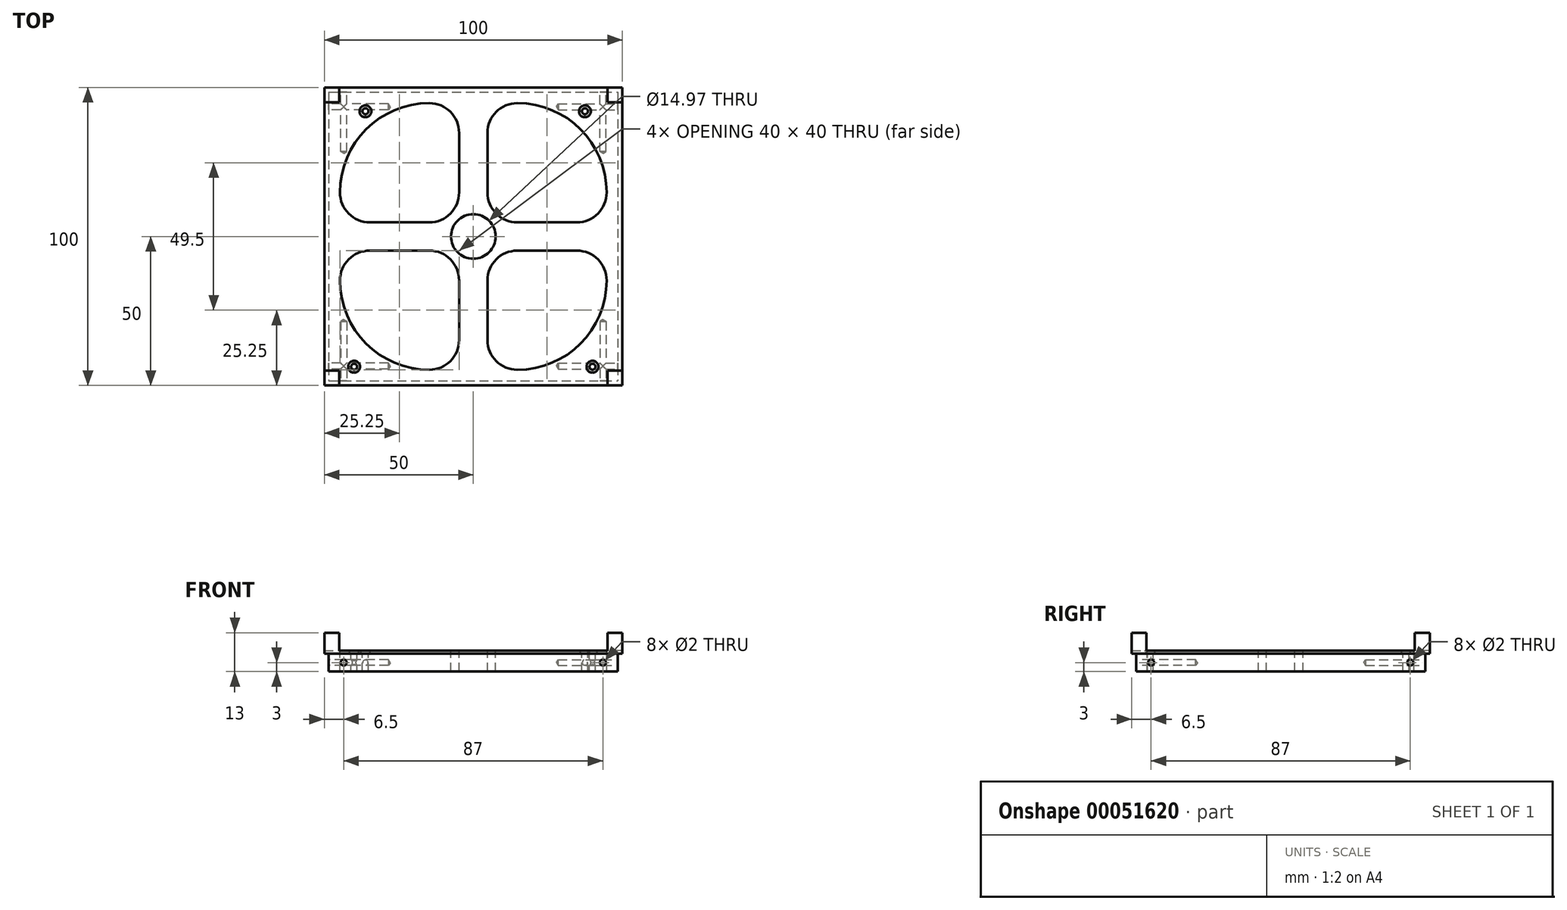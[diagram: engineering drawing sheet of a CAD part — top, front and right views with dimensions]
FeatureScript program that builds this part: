
annotation { "Feature Type Name" : "Feature", "Feature Type Description" : "" }
export const myFeature = defineFeature(function(context is Context, id is Id, definition is map)
    precondition{}
    {
        {
            var Q0;
            Q0=qCreatedBy(makeId("Top.planeOp"),FACE);
            var sketch = newSketch(context, id + "F0", { "sketchPlane" : qUnion([Q0])});
            skLineSegment(sketch, "E0.rect.bottom", {"start": v(-50, 50) * mm, "end": v(50, 50) * mm});
            skLineSegment(sketch, "E0.rect.top", {"start": v(-50, -50) * mm, "end": v(50, -50) * mm});
            skLineSegment(sketch, "E0.rect.left", {"start": v(-50, 50) * mm, "end": v(-50, -50) * mm});
            skLineSegment(sketch, "E0.rect.right", {"start": v(50, 50) * mm, "end": v(50, -50) * mm});
            skPoint(sketch, "E0.rect.middle", {"position": v(0, 0) * mm});
            skLineSegment(sketch, "E1.rect.bottom", {"start": v(-48.5, 48.5) * mm, "end": v(48.5, 48.5) * mm});
            skLineSegment(sketch, "E1.rect.top", {"start": v(-48.5, -48.5) * mm, "end": v(48.5, -48.5) * mm});
            skLineSegment(sketch, "E1.rect.left", {"start": v(-48.5, 48.5) * mm, "end": v(-48.5, -48.5) * mm});
            skLineSegment(sketch, "E1.rect.right", {"start": v(48.5, 48.5) * mm, "end": v(48.5, -48.5) * mm});
            skLineSegment(sketch, "E2.rect.bottom", {"start": v(-14.75, 4.75) * mm, "end": v(-34.75, 4.75) * mm});
            skLineSegment(sketch, "E2.rect.top", {"start": v(-14.75, 44.75) * mm, "end": v(-14.75, 44.75) * mm});
            skLineSegment(sketch, "E2.rect.left", {"start": v(-4.75, 14.75) * mm, "end": v(-4.75, 34.75) * mm});
            skLineSegment(sketch, "E2.rect.right", {"start": v(-44.75, 14.75) * mm, "end": v(-44.75, 14.75) * mm});
            skPoint(sketch, "E2.rect.middle", {"position": v(-24.75, 24.75) * mm});
            skPoint(sketch, "E3.visualSharp", {"position": v(-44.75, 44.75) * mm});
            skArc(sketch, "E3.filletArc", {"start": v(-14.75, 44.75) * mm, "mid": v(-35.96, 35.96) * mm, "end": v(-44.75, 14.75) * mm});
            skPoint(sketch, "E4.visualSharp", {"position": v(-4.75, 44.75) * mm});
            skArc(sketch, "E4.filletArc", {"start": v(-4.75, 34.75) * mm, "mid": v(-7.68, 41.82) * mm, "end": v(-14.75, 44.75) * mm});
            skPoint(sketch, "E5.visualSharp", {"position": v(-4.75, 4.75) * mm});
            skArc(sketch, "E5.filletArc", {"start": v(-14.75, 4.75) * mm, "mid": v(-7.68, 7.68) * mm, "end": v(-4.75, 14.75) * mm});
            skPoint(sketch, "E6.visualSharp", {"position": v(-44.75, 4.75) * mm});
            skArc(sketch, "E6.filletArc", {"start": v(-44.75, 14.75) * mm, "mid": v(-41.82, 7.68) * mm, "end": v(-34.75, 4.75) * mm});
            skLineSegment(sketch, "E7.MirrorCS", {"start": v(4.75, 14.75) * mm, "end": v(4.75, 34.75) * mm});
            skArc(sketch, "E8.MirrorCS", {"start": v(4.75, 34.75) * mm, "mid": v(7.68, 41.82) * mm, "end": v(14.75, 44.75) * mm});
            skLineSegment(sketch, "E9.MirrorCS", {"start": v(14.75, 44.75) * mm, "end": v(14.75, 44.75) * mm});
            skArc(sketch, "E10.MirrorCS", {"start": v(14.75, 44.75) * mm, "mid": v(35.96, 35.96) * mm, "end": v(44.75, 14.75) * mm});
            skLineSegment(sketch, "E11.MirrorCS", {"start": v(44.75, 14.75) * mm, "end": v(44.75, 14.75) * mm});
            skArc(sketch, "E12.MirrorCS", {"start": v(44.75, 14.75) * mm, "mid": v(41.82, 7.68) * mm, "end": v(34.75, 4.75) * mm});
            skLineSegment(sketch, "E13.MirrorCS", {"start": v(14.75, 4.75) * mm, "end": v(34.75, 4.75) * mm});
            skArc(sketch, "E14.MirrorCS", {"start": v(14.75, 4.75) * mm, "mid": v(7.68, 7.68) * mm, "end": v(4.75, 14.75) * mm});
            skPoint(sketch, "E15.MirrorP", {"position": v(24.75, 24.75) * mm});
            skArc(sketch, "E16.MirrorCS", {"start": v(14.75, -4.75) * mm, "mid": v(7.68, -7.68) * mm, "end": v(4.75, -14.75) * mm});
            skLineSegment(sketch, "E17.MirrorCS", {"start": v(4.75, -14.75) * mm, "end": v(4.75, -34.75) * mm});
            skArc(sketch, "E18.MirrorCS", {"start": v(4.75, -34.75) * mm, "mid": v(7.68, -41.82) * mm, "end": v(14.75, -44.75) * mm});
            skLineSegment(sketch, "E19.MirrorCS", {"start": v(14.75, -44.75) * mm, "end": v(14.75, -44.75) * mm});
            skArc(sketch, "E20.MirrorCS", {"start": v(14.75, -44.75) * mm, "mid": v(35.96, -35.96) * mm, "end": v(44.75, -14.75) * mm});
            skLineSegment(sketch, "E21.MirrorCS", {"start": v(44.75, -14.75) * mm, "end": v(44.75, -14.75) * mm});
            skArc(sketch, "E22.MirrorCS", {"start": v(44.75, -14.75) * mm, "mid": v(41.82, -7.68) * mm, "end": v(34.75, -4.75) * mm});
            skLineSegment(sketch, "E23.MirrorCS", {"start": v(14.75, -4.75) * mm, "end": v(34.75, -4.75) * mm});
            skPoint(sketch, "E24.MirrorP", {"position": v(24.75, -24.75) * mm});
            skLineSegment(sketch, "E25.MirrorCS", {"start": v(-4.75, -14.75) * mm, "end": v(-4.75, -34.75) * mm});
            skArc(sketch, "E26.MirrorCS", {"start": v(-14.75, -4.75) * mm, "mid": v(-7.68, -7.68) * mm, "end": v(-4.75, -14.75) * mm});
            skLineSegment(sketch, "E27.MirrorCS", {"start": v(-14.75, -4.75) * mm, "end": v(-34.75, -4.75) * mm});
            skArc(sketch, "E28.MirrorCS", {"start": v(-44.75, -14.75) * mm, "mid": v(-41.82, -7.68) * mm, "end": v(-34.75, -4.75) * mm});
            skLineSegment(sketch, "E29.MirrorCS", {"start": v(-44.75, -14.75) * mm, "end": v(-44.75, -14.75) * mm});
            skArc(sketch, "E30.MirrorCS", {"start": v(-14.75, -44.75) * mm, "mid": v(-35.96, -35.96) * mm, "end": v(-44.75, -14.75) * mm});
            skLineSegment(sketch, "E31.MirrorCS", {"start": v(-14.75, -44.75) * mm, "end": v(-14.75, -44.75) * mm});
            skArc(sketch, "E32.MirrorCS", {"start": v(-4.75, -34.75) * mm, "mid": v(-7.68, -41.82) * mm, "end": v(-14.75, -44.75) * mm});
            skPoint(sketch, "E33.MirrorP", {"position": v(-24.75, -24.75) * mm});
            skPoint(sketch, "E34", {"position": v(42.5, -42.5) * mm});
            skPoint(sketch, "E35.MirrorP", {"position": v(-42.5, -42.5) * mm});
            skPoint(sketch, "E36.MirrorP", {"position": v(42.5, 42.5) * mm});
            skPoint(sketch, "E37.MirrorP", {"position": v(-42.5, 42.5) * mm});
            skCircle(sketch, "E38", {"center": v(0, 0) * mm, "radius": 7.48 * mm});
            skSolve(sketch);
        }
        {
            var Q0;
            Q0=makeQuery(id+"F0.imprint","IMPRINT",FACE,{"disambiguationData":[TD([[makeQuery(id+"F0.imprint","IMPRINT",EDGE,{"derivedFrom":sQuery(id+"F0.wireOp",EDGE,"E1.rect.bottom")}),-1.0]])]});
            extrude(context, id + "F1", {"entities" : qUnion([Q0]), "oppositeDirection" : true, "depth" : 6 * mm});
        }
        {
            var Q0;
            Q0=qSketchRegion(id+"F0",true);
            var Q1;
            Q1=makeQuery(id+"F1.opExtrude","CAP_FACE",FACE,{"disambiguationData":[OSD([sQuery(id+"F0.wireOp",EDGE,"E1.rect.bottom"),sQuery(id+"F0.wireOp",EDGE,"E1.rect.top"),sQuery(id+"F0.wireOp",EDGE,"E1.rect.left"),sQuery(id+"F0.wireOp",EDGE,"E1.rect.right"),sQuery(id+"F0.wireOp",EDGE,"E2.rect.bottom"),sQuery(id+"F0.wireOp",EDGE,"E2.rect.top"),sQuery(id+"F0.wireOp",EDGE,"E2.rect.left"),sQuery(id+"F0.wireOp",EDGE,"E2.rect.right"),sQuery(id+"F0.wireOp",EDGE,"d764ca65-7f6a-4e13-98eb-a7907a3d072d0.MirrorCS"),sQuery(id+"F0.wireOp",EDGE,"4e8c5bec-c53d-4312-8259-349e49f543fe0.MirrorCS"),sQuery(id+"F0.wireOp",EDGE,"d6a0bf7c-e4bc-484e-b3d5-183d898144500.MirrorCS"),sQuery(id+"F0.wireOp",EDGE,"45a758ec-378c-46c5-b086-a70cc1cacffd0.MirrorCS"),sQuery(id+"F0.wireOp",EDGE,"a64d5360-d78c-41ef-9f44-8c8436a09bba0.MirrorCS"),sQuery(id+"F0.wireOp",EDGE,"c998a958-b69a-464e-a296-dd7f6d349ec80.MirrorCS"),sQuery(id+"F0.wireOp",EDGE,"a4bf1b2a-a2f4-4ab3-9d73-85797b196d270.MirrorCS"),sQuery(id+"F0.wireOp",EDGE,"ecd2f3fb-4ea3-4913-80f4-94ebebe2d04e0.MirrorCS"),sQuery(id+"F0.wireOp",EDGE,"085a2cb5-2e3f-4cc3-a5b9-01c6e75669f10.MirrorCS"),sQuery(id+"F0.wireOp",EDGE,"73d67a52-dadc-4bd6-8141-d25047cb753b0.MirrorCS"),sQuery(id+"F0.wireOp",EDGE,"8f6832c0-858d-4205-8574-29f35786d1620.MirrorCS"),sQuery(id+"F0.wireOp",EDGE,"ecc9a695-4792-4055-9804-abf58933c5b20.MirrorCS")])],"isStart":false});
            extrude(context, id + "F2", {"entities" : qUnion([Q0, Q1]), "operationType" : NewBodyOperationType.ADD, "oppositeDirection" : true, "depth" : 1 * mm});
        }
        {
            var Q0;
            {var subQ0=sQuery(id+"F0.wireOp",EDGE,"E1.rect.bottom");Q0=makeQuery(id+"F2.boolean.opBoolean","MERGE",FACE,{"derivedFrom":[makeQuery(id+"F1.opExtrude","SWEPT_FACE",FACE,{"disambiguationData":[OSD([subQ0])]}),makeQuery(id+"F2.opExtrude","SWEPT_FACE",FACE,{"disambiguationData":[OSD([subQ0]),TDD([makeQuery(id+"F1.opExtrude","CAP_EDGE",EDGE,{"disambiguationData":[OSD([subQ0])],"isStart":false})])]})]});}
            var sketch = newSketch(context, id + "F3", { "sketchPlane" : qUnion([Q0])});
            skPoint(sketch, "E39", {"position": v(-43.5, -4) * mm});
            skPoint(sketch, "E40.MirrorP", {"position": v(43.5, -4) * mm});
            skSolve(sketch);
        }
        {
            var Q0;
            Q0=sQuery(id+"F3.wireOp",VERTEX,"E39");
            var Q1;
            Q1=sQuery(id+"F3.wireOp",VERTEX,"E40.MirrorP");
            var Q2;
            Q2=makeQuery(id+"F1.opExtrude","SWEPT_BODY",BODY,{"disambiguationData":[OSD([sQuery(id+"F0.wireOp",EDGE,"E1.rect.bottom"),sQuery(id+"F0.wireOp",EDGE,"E1.rect.top"),sQuery(id+"F0.wireOp",EDGE,"E1.rect.left"),sQuery(id+"F0.wireOp",EDGE,"E1.rect.right"),sQuery(id+"F0.wireOp",EDGE,"E2.rect.bottom"),sQuery(id+"F0.wireOp",EDGE,"E2.rect.top"),sQuery(id+"F0.wireOp",EDGE,"E2.rect.left"),sQuery(id+"F0.wireOp",EDGE,"E2.rect.right"),sQuery(id+"F0.wireOp",EDGE,"E3.filletArc"),sQuery(id+"F0.wireOp",EDGE,"E4.filletArc"),sQuery(id+"F0.wireOp",EDGE,"E5.filletArc"),sQuery(id+"F0.wireOp",EDGE,"E6.filletArc"),sQuery(id+"F0.wireOp",EDGE,"E7.MirrorCS"),sQuery(id+"F0.wireOp",EDGE,"E8.MirrorCS"),sQuery(id+"F0.wireOp",EDGE,"E9.MirrorCS"),sQuery(id+"F0.wireOp",EDGE,"E10.MirrorCS"),sQuery(id+"F0.wireOp",EDGE,"E11.MirrorCS"),sQuery(id+"F0.wireOp",EDGE,"E12.MirrorCS"),sQuery(id+"F0.wireOp",EDGE,"E13.MirrorCS"),sQuery(id+"F0.wireOp",EDGE,"E14.MirrorCS"),sQuery(id+"F0.wireOp",EDGE,"E16.MirrorCS"),sQuery(id+"F0.wireOp",EDGE,"E17.MirrorCS"),sQuery(id+"F0.wireOp",EDGE,"E18.MirrorCS"),sQuery(id+"F0.wireOp",EDGE,"E19.MirrorCS"),sQuery(id+"F0.wireOp",EDGE,"E20.MirrorCS"),sQuery(id+"F0.wireOp",EDGE,"E21.MirrorCS"),sQuery(id+"F0.wireOp",EDGE,"E22.MirrorCS"),sQuery(id+"F0.wireOp",EDGE,"E23.MirrorCS"),sQuery(id+"F0.wireOp",EDGE,"E25.MirrorCS"),sQuery(id+"F0.wireOp",EDGE,"E26.MirrorCS"),sQuery(id+"F0.wireOp",EDGE,"E27.MirrorCS"),sQuery(id+"F0.wireOp",EDGE,"E28.MirrorCS"),sQuery(id+"F0.wireOp",EDGE,"E29.MirrorCS"),sQuery(id+"F0.wireOp",EDGE,"E30.MirrorCS"),sQuery(id+"F0.wireOp",EDGE,"E31.MirrorCS"),sQuery(id+"F0.wireOp",EDGE,"E32.MirrorCS")])]});
            hole(context, id + "F4", {"style" : HoleStyle.SIMPLE, "holeDiameter" : 2 * mm, "endStyle" : HoleEndStyle.BLIND, "holeDepth" : 20 * mm, "locations" : qUnion([Q0, Q1]), "scope" : qUnion([Q2])});
        }
        {
            var Q0;
            {var subQ0=sQuery(id+"F0.wireOp",EDGE,"E1.rect.left");Q0=makeQuery(id+"F2.boolean.opBoolean","MERGE",FACE,{"derivedFrom":[makeQuery(id+"F1.opExtrude","SWEPT_FACE",FACE,{"disambiguationData":[OSD([subQ0])]}),makeQuery(id+"F2.opExtrude","SWEPT_FACE",FACE,{"disambiguationData":[OSD([subQ0]),TDD([makeQuery(id+"F1.opExtrude","CAP_EDGE",EDGE,{"disambiguationData":[OSD([subQ0])],"isStart":false})])]})]});}
            var sketch = newSketch(context, id + "F5", { "sketchPlane" : qUnion([Q0])});
            skPoint(sketch, "E41", {"position": v(-43.5, -4) * mm});
            skPoint(sketch, "E42.MirrorP", {"position": v(43.5, -4) * mm});
            skSolve(sketch);
        }
        {
            var Q0;
            Q0=sQuery(id+"F5.wireOp",VERTEX,"E41");
            var Q1;
            Q1=sQuery(id+"F5.wireOp",VERTEX,"E42.MirrorP");
            var Q2;
            Q2=makeQuery(id+"F1.opExtrude","SWEPT_BODY",BODY,{"disambiguationData":[OSD([sQuery(id+"F0.wireOp",EDGE,"E1.rect.bottom"),sQuery(id+"F0.wireOp",EDGE,"E1.rect.top"),sQuery(id+"F0.wireOp",EDGE,"E1.rect.left"),sQuery(id+"F0.wireOp",EDGE,"E1.rect.right"),sQuery(id+"F0.wireOp",EDGE,"E2.rect.bottom"),sQuery(id+"F0.wireOp",EDGE,"E2.rect.top"),sQuery(id+"F0.wireOp",EDGE,"E2.rect.left"),sQuery(id+"F0.wireOp",EDGE,"E2.rect.right"),sQuery(id+"F0.wireOp",EDGE,"E3.filletArc"),sQuery(id+"F0.wireOp",EDGE,"E4.filletArc"),sQuery(id+"F0.wireOp",EDGE,"E5.filletArc"),sQuery(id+"F0.wireOp",EDGE,"E6.filletArc"),sQuery(id+"F0.wireOp",EDGE,"E7.MirrorCS"),sQuery(id+"F0.wireOp",EDGE,"E8.MirrorCS"),sQuery(id+"F0.wireOp",EDGE,"E9.MirrorCS"),sQuery(id+"F0.wireOp",EDGE,"E10.MirrorCS"),sQuery(id+"F0.wireOp",EDGE,"E11.MirrorCS"),sQuery(id+"F0.wireOp",EDGE,"E12.MirrorCS"),sQuery(id+"F0.wireOp",EDGE,"E13.MirrorCS"),sQuery(id+"F0.wireOp",EDGE,"E14.MirrorCS"),sQuery(id+"F0.wireOp",EDGE,"E16.MirrorCS"),sQuery(id+"F0.wireOp",EDGE,"E17.MirrorCS"),sQuery(id+"F0.wireOp",EDGE,"E18.MirrorCS"),sQuery(id+"F0.wireOp",EDGE,"E19.MirrorCS"),sQuery(id+"F0.wireOp",EDGE,"E20.MirrorCS"),sQuery(id+"F0.wireOp",EDGE,"E21.MirrorCS"),sQuery(id+"F0.wireOp",EDGE,"E22.MirrorCS"),sQuery(id+"F0.wireOp",EDGE,"E23.MirrorCS"),sQuery(id+"F0.wireOp",EDGE,"E25.MirrorCS"),sQuery(id+"F0.wireOp",EDGE,"E26.MirrorCS"),sQuery(id+"F0.wireOp",EDGE,"E27.MirrorCS"),sQuery(id+"F0.wireOp",EDGE,"E28.MirrorCS"),sQuery(id+"F0.wireOp",EDGE,"E29.MirrorCS"),sQuery(id+"F0.wireOp",EDGE,"E30.MirrorCS"),sQuery(id+"F0.wireOp",EDGE,"E31.MirrorCS"),sQuery(id+"F0.wireOp",EDGE,"E32.MirrorCS")])]});
            hole(context, id + "F6", {"style" : HoleStyle.SIMPLE, "holeDiameter" : 2 * mm, "endStyle" : HoleEndStyle.BLIND, "holeDepth" : 20 * mm, "locations" : qUnion([Q0, Q1]), "scope" : qUnion([Q2])});
        }
        {
            var Q0;
            {var subQ0=sQuery(id+"F0.wireOp",EDGE,"E1.rect.top");Q0=makeQuery(id+"F2.boolean.opBoolean","MERGE",FACE,{"derivedFrom":[makeQuery(id+"F1.opExtrude","SWEPT_FACE",FACE,{"disambiguationData":[OSD([subQ0])]}),makeQuery(id+"F2.opExtrude","SWEPT_FACE",FACE,{"disambiguationData":[OSD([subQ0]),TDD([makeQuery(id+"F1.opExtrude","CAP_EDGE",EDGE,{"disambiguationData":[OSD([subQ0])],"isStart":false})])]})]});}
            var sketch = newSketch(context, id + "F7", { "sketchPlane" : qUnion([Q0])});
            skPoint(sketch, "E43", {"position": v(-43.5, -4) * mm});
            skPoint(sketch, "E44.MirrorP", {"position": v(43.5, -4) * mm});
            skSolve(sketch);
        }
        {
            var Q0;
            Q0=sQuery(id+"F7.wireOp",VERTEX,"E43");
            var Q1;
            Q1=sQuery(id+"F7.wireOp",VERTEX,"E44.MirrorP");
            var Q2;
            Q2=makeQuery(id+"F1.opExtrude","SWEPT_BODY",BODY,{"disambiguationData":[OSD([sQuery(id+"F0.wireOp",EDGE,"E1.rect.bottom"),sQuery(id+"F0.wireOp",EDGE,"E1.rect.top"),sQuery(id+"F0.wireOp",EDGE,"E1.rect.left"),sQuery(id+"F0.wireOp",EDGE,"E1.rect.right"),sQuery(id+"F0.wireOp",EDGE,"E2.rect.bottom"),sQuery(id+"F0.wireOp",EDGE,"E2.rect.top"),sQuery(id+"F0.wireOp",EDGE,"E2.rect.left"),sQuery(id+"F0.wireOp",EDGE,"E2.rect.right"),sQuery(id+"F0.wireOp",EDGE,"E3.filletArc"),sQuery(id+"F0.wireOp",EDGE,"E4.filletArc"),sQuery(id+"F0.wireOp",EDGE,"E5.filletArc"),sQuery(id+"F0.wireOp",EDGE,"E6.filletArc"),sQuery(id+"F0.wireOp",EDGE,"E7.MirrorCS"),sQuery(id+"F0.wireOp",EDGE,"E8.MirrorCS"),sQuery(id+"F0.wireOp",EDGE,"E9.MirrorCS"),sQuery(id+"F0.wireOp",EDGE,"E10.MirrorCS"),sQuery(id+"F0.wireOp",EDGE,"E11.MirrorCS"),sQuery(id+"F0.wireOp",EDGE,"E12.MirrorCS"),sQuery(id+"F0.wireOp",EDGE,"E13.MirrorCS"),sQuery(id+"F0.wireOp",EDGE,"E14.MirrorCS"),sQuery(id+"F0.wireOp",EDGE,"E16.MirrorCS"),sQuery(id+"F0.wireOp",EDGE,"E17.MirrorCS"),sQuery(id+"F0.wireOp",EDGE,"E18.MirrorCS"),sQuery(id+"F0.wireOp",EDGE,"E19.MirrorCS"),sQuery(id+"F0.wireOp",EDGE,"E20.MirrorCS"),sQuery(id+"F0.wireOp",EDGE,"E21.MirrorCS"),sQuery(id+"F0.wireOp",EDGE,"E22.MirrorCS"),sQuery(id+"F0.wireOp",EDGE,"E23.MirrorCS"),sQuery(id+"F0.wireOp",EDGE,"E25.MirrorCS"),sQuery(id+"F0.wireOp",EDGE,"E26.MirrorCS"),sQuery(id+"F0.wireOp",EDGE,"E27.MirrorCS"),sQuery(id+"F0.wireOp",EDGE,"E28.MirrorCS"),sQuery(id+"F0.wireOp",EDGE,"E29.MirrorCS"),sQuery(id+"F0.wireOp",EDGE,"E30.MirrorCS"),sQuery(id+"F0.wireOp",EDGE,"E31.MirrorCS"),sQuery(id+"F0.wireOp",EDGE,"E32.MirrorCS")])]});
            hole(context, id + "F8", {"style" : HoleStyle.SIMPLE, "holeDiameter" : 2 * mm, "endStyle" : HoleEndStyle.BLIND, "holeDepth" : 20 * mm, "locations" : qUnion([Q0, Q1]), "scope" : qUnion([Q2])});
        }
        {
            var Q0;
            {var subQ0=sQuery(id+"F0.wireOp",EDGE,"E1.rect.right");Q0=makeQuery(id+"F2.boolean.opBoolean","MERGE",FACE,{"derivedFrom":[makeQuery(id+"F1.opExtrude","SWEPT_FACE",FACE,{"disambiguationData":[OSD([subQ0])]}),makeQuery(id+"F2.opExtrude","SWEPT_FACE",FACE,{"disambiguationData":[OSD([subQ0]),TDD([makeQuery(id+"F1.opExtrude","CAP_EDGE",EDGE,{"disambiguationData":[OSD([subQ0])],"isStart":false})])]})]});}
            var sketch = newSketch(context, id + "F9", { "sketchPlane" : qUnion([Q0])});
            skPoint(sketch, "E45", {"position": v(-43.5, -4) * mm});
            skPoint(sketch, "E46.MirrorP", {"position": v(43.5, -4) * mm});
            skSolve(sketch);
        }
        {
            var Q0;
            Q0=sQuery(id+"F9.wireOp",VERTEX,"E45");
            var Q1;
            Q1=sQuery(id+"F9.wireOp",VERTEX,"E46.MirrorP");
            var Q2;
            Q2=makeQuery(id+"F1.opExtrude","SWEPT_BODY",BODY,{"disambiguationData":[OSD([sQuery(id+"F0.wireOp",EDGE,"E1.rect.bottom"),sQuery(id+"F0.wireOp",EDGE,"E1.rect.top"),sQuery(id+"F0.wireOp",EDGE,"E1.rect.left"),sQuery(id+"F0.wireOp",EDGE,"E1.rect.right"),sQuery(id+"F0.wireOp",EDGE,"E2.rect.bottom"),sQuery(id+"F0.wireOp",EDGE,"E2.rect.top"),sQuery(id+"F0.wireOp",EDGE,"E2.rect.left"),sQuery(id+"F0.wireOp",EDGE,"E2.rect.right"),sQuery(id+"F0.wireOp",EDGE,"E3.filletArc"),sQuery(id+"F0.wireOp",EDGE,"E4.filletArc"),sQuery(id+"F0.wireOp",EDGE,"E5.filletArc"),sQuery(id+"F0.wireOp",EDGE,"E6.filletArc"),sQuery(id+"F0.wireOp",EDGE,"E7.MirrorCS"),sQuery(id+"F0.wireOp",EDGE,"E8.MirrorCS"),sQuery(id+"F0.wireOp",EDGE,"E9.MirrorCS"),sQuery(id+"F0.wireOp",EDGE,"E10.MirrorCS"),sQuery(id+"F0.wireOp",EDGE,"E11.MirrorCS"),sQuery(id+"F0.wireOp",EDGE,"E12.MirrorCS"),sQuery(id+"F0.wireOp",EDGE,"E13.MirrorCS"),sQuery(id+"F0.wireOp",EDGE,"E14.MirrorCS"),sQuery(id+"F0.wireOp",EDGE,"E16.MirrorCS"),sQuery(id+"F0.wireOp",EDGE,"E17.MirrorCS"),sQuery(id+"F0.wireOp",EDGE,"E18.MirrorCS"),sQuery(id+"F0.wireOp",EDGE,"E19.MirrorCS"),sQuery(id+"F0.wireOp",EDGE,"E20.MirrorCS"),sQuery(id+"F0.wireOp",EDGE,"E21.MirrorCS"),sQuery(id+"F0.wireOp",EDGE,"E22.MirrorCS"),sQuery(id+"F0.wireOp",EDGE,"E23.MirrorCS"),sQuery(id+"F0.wireOp",EDGE,"E25.MirrorCS"),sQuery(id+"F0.wireOp",EDGE,"E26.MirrorCS"),sQuery(id+"F0.wireOp",EDGE,"E27.MirrorCS"),sQuery(id+"F0.wireOp",EDGE,"E28.MirrorCS"),sQuery(id+"F0.wireOp",EDGE,"E29.MirrorCS"),sQuery(id+"F0.wireOp",EDGE,"E30.MirrorCS"),sQuery(id+"F0.wireOp",EDGE,"E31.MirrorCS"),sQuery(id+"F0.wireOp",EDGE,"E32.MirrorCS")])]});
            hole(context, id + "F10", {"style" : HoleStyle.SIMPLE, "holeDiameter" : 2 * mm, "endStyle" : HoleEndStyle.BLIND, "holeDepth" : 20 * mm, "locations" : qUnion([Q0, Q1]), "scope" : qUnion([Q2])});
        }
        {
            var Q0;
            {var subQ0=sQuery(id+"F0.wireOp",EDGE,"E1.rect.bottom");var subQ1=sQuery(id+"F0.wireOp",EDGE,"E1.rect.top");var subQ2=sQuery(id+"F0.wireOp",EDGE,"E1.rect.left");var subQ3=sQuery(id+"F0.wireOp",EDGE,"E1.rect.right");Q0=makeQuery(id+"F2.boolean.opBoolean","MERGE",FACE,{"derivedFrom":[makeQuery(id+"F1.opExtrude","CAP_FACE",FACE,{"disambiguationData":[OSD([subQ0,subQ1,subQ2,subQ3,sQuery(id+"F0.wireOp",EDGE,"E2.rect.bottom"),sQuery(id+"F0.wireOp",EDGE,"E2.rect.top"),sQuery(id+"F0.wireOp",EDGE,"E2.rect.left"),sQuery(id+"F0.wireOp",EDGE,"E2.rect.right"),sQuery(id+"F0.wireOp",EDGE,"E3.filletArc"),sQuery(id+"F0.wireOp",EDGE,"E4.filletArc"),sQuery(id+"F0.wireOp",EDGE,"E5.filletArc"),sQuery(id+"F0.wireOp",EDGE,"E6.filletArc"),sQuery(id+"F0.wireOp",EDGE,"E7.MirrorCS"),sQuery(id+"F0.wireOp",EDGE,"E8.MirrorCS"),sQuery(id+"F0.wireOp",EDGE,"E9.MirrorCS"),sQuery(id+"F0.wireOp",EDGE,"E10.MirrorCS"),sQuery(id+"F0.wireOp",EDGE,"E11.MirrorCS"),sQuery(id+"F0.wireOp",EDGE,"E12.MirrorCS"),sQuery(id+"F0.wireOp",EDGE,"E13.MirrorCS"),sQuery(id+"F0.wireOp",EDGE,"E14.MirrorCS"),sQuery(id+"F0.wireOp",EDGE,"E16.MirrorCS"),sQuery(id+"F0.wireOp",EDGE,"E17.MirrorCS"),sQuery(id+"F0.wireOp",EDGE,"E18.MirrorCS"),sQuery(id+"F0.wireOp",EDGE,"E19.MirrorCS"),sQuery(id+"F0.wireOp",EDGE,"E20.MirrorCS"),sQuery(id+"F0.wireOp",EDGE,"E21.MirrorCS"),sQuery(id+"F0.wireOp",EDGE,"E22.MirrorCS"),sQuery(id+"F0.wireOp",EDGE,"E23.MirrorCS"),sQuery(id+"F0.wireOp",EDGE,"E25.MirrorCS"),sQuery(id+"F0.wireOp",EDGE,"E26.MirrorCS"),sQuery(id+"F0.wireOp",EDGE,"E27.MirrorCS"),sQuery(id+"F0.wireOp",EDGE,"E28.MirrorCS"),sQuery(id+"F0.wireOp",EDGE,"E29.MirrorCS"),sQuery(id+"F0.wireOp",EDGE,"E30.MirrorCS"),sQuery(id+"F0.wireOp",EDGE,"E31.MirrorCS"),sQuery(id+"F0.wireOp",EDGE,"E32.MirrorCS")])],"isStart":true}),makeQuery(id+"F2.opExtrude","CAP_FACE",FACE,{"disambiguationData":[OSD([sQuery(id+"F0.wireOp",EDGE,"E0.rect.bottom"),sQuery(id+"F0.wireOp",EDGE,"E0.rect.top"),sQuery(id+"F0.wireOp",EDGE,"E0.rect.left"),sQuery(id+"F0.wireOp",EDGE,"E0.rect.right"),subQ0,subQ1,subQ2,subQ3])],"isStart":true})]});}
            var sketch = newSketch(context, id + "F11", { "sketchPlane" : qUnion([Q0])});
            skPoint(sketch, "E47", {"position": v(-36.2, -129.45) * mm});
            skPoint(sketch, "E48", {"position": v(40, -43.72) * mm});
            skPoint(sketch, "E49", {"position": v(37.47, -129.45) * mm});
            skPoint(sketch, "E50", {"position": v(-40, -43.72) * mm});
            skPoint(sketch, "E51", {"position": v(-36.2, 42.01) * mm});
            skPoint(sketch, "E52", {"position": v(37.46, 42.01) * mm});
            skLineSegment(sketch, "E53.bottom", {"start": v(50, 50) * mm, "end": v(45, 50) * mm});
            skLineSegment(sketch, "E53.top", {"start": v(50, 45) * mm, "end": v(45, 45) * mm});
            skLineSegment(sketch, "E53.left", {"start": v(50, 50) * mm, "end": v(50, 45) * mm});
            skLineSegment(sketch, "E53.right", {"start": v(45, 50) * mm, "end": v(45, 45) * mm});
            skLineSegment(sketch, "E54.MirrorCS", {"start": v(-45, 50) * mm, "end": v(-45, 45) * mm});
            skLineSegment(sketch, "E55.MirrorCS", {"start": v(-50, 50) * mm, "end": v(-50, 45) * mm});
            skLineSegment(sketch, "E56.MirrorCS", {"start": v(-50, 45) * mm, "end": v(-45, 45) * mm});
            skLineSegment(sketch, "E57.MirrorCS", {"start": v(-50, 50) * mm, "end": v(-45, 50) * mm});
            skLineSegment(sketch, "E58.MirrorCS", {"start": v(50, -45) * mm, "end": v(45, -45) * mm});
            skLineSegment(sketch, "E59.MirrorCS", {"start": v(50, -50) * mm, "end": v(45, -50) * mm});
            skLineSegment(sketch, "E60.MirrorCS", {"start": v(50, -50) * mm, "end": v(50, -45) * mm});
            skLineSegment(sketch, "E61.MirrorCS", {"start": v(45, -50) * mm, "end": v(45, -45) * mm});
            skLineSegment(sketch, "E62.MirrorCS", {"start": v(-50, -50) * mm, "end": v(-50, -45) * mm});
            skLineSegment(sketch, "E63.MirrorCS", {"start": v(-45, -50) * mm, "end": v(-45, -45) * mm});
            skLineSegment(sketch, "E64.MirrorCS", {"start": v(-50, -45) * mm, "end": v(-45, -45) * mm});
            skLineSegment(sketch, "E65.MirrorCS", {"start": v(-50, -50) * mm, "end": v(-45, -50) * mm});
            skSolve(sketch);
        }
        {
            var Q0;
            Q0=sQuery(id+"F11.wireOp",VERTEX,"E52");
            var Q1;
            Q1=sQuery(id+"F11.wireOp",VERTEX,"E51");
            var Q2;
            Q2=sQuery(id+"F11.wireOp",VERTEX,"E48");
            var Q3;
            Q3=sQuery(id+"F11.wireOp",VERTEX,"E50");
            var Q4;
            Q4=makeQuery(id+"F1.opExtrude","SWEPT_BODY",BODY,{"disambiguationData":[OSD([sQuery(id+"F0.wireOp",EDGE,"E1.rect.bottom"),sQuery(id+"F0.wireOp",EDGE,"E1.rect.top"),sQuery(id+"F0.wireOp",EDGE,"E1.rect.left"),sQuery(id+"F0.wireOp",EDGE,"E1.rect.right"),sQuery(id+"F0.wireOp",EDGE,"E2.rect.bottom"),sQuery(id+"F0.wireOp",EDGE,"E2.rect.top"),sQuery(id+"F0.wireOp",EDGE,"E2.rect.left"),sQuery(id+"F0.wireOp",EDGE,"E2.rect.right"),sQuery(id+"F0.wireOp",EDGE,"E3.filletArc"),sQuery(id+"F0.wireOp",EDGE,"E4.filletArc"),sQuery(id+"F0.wireOp",EDGE,"E5.filletArc"),sQuery(id+"F0.wireOp",EDGE,"E6.filletArc"),sQuery(id+"F0.wireOp",EDGE,"E7.MirrorCS"),sQuery(id+"F0.wireOp",EDGE,"E8.MirrorCS"),sQuery(id+"F0.wireOp",EDGE,"E9.MirrorCS"),sQuery(id+"F0.wireOp",EDGE,"E10.MirrorCS"),sQuery(id+"F0.wireOp",EDGE,"E11.MirrorCS"),sQuery(id+"F0.wireOp",EDGE,"E12.MirrorCS"),sQuery(id+"F0.wireOp",EDGE,"E13.MirrorCS"),sQuery(id+"F0.wireOp",EDGE,"E14.MirrorCS"),sQuery(id+"F0.wireOp",EDGE,"E16.MirrorCS"),sQuery(id+"F0.wireOp",EDGE,"E17.MirrorCS"),sQuery(id+"F0.wireOp",EDGE,"E18.MirrorCS"),sQuery(id+"F0.wireOp",EDGE,"E19.MirrorCS"),sQuery(id+"F0.wireOp",EDGE,"E20.MirrorCS"),sQuery(id+"F0.wireOp",EDGE,"E21.MirrorCS"),sQuery(id+"F0.wireOp",EDGE,"E22.MirrorCS"),sQuery(id+"F0.wireOp",EDGE,"E23.MirrorCS"),sQuery(id+"F0.wireOp",EDGE,"E25.MirrorCS"),sQuery(id+"F0.wireOp",EDGE,"E26.MirrorCS"),sQuery(id+"F0.wireOp",EDGE,"E27.MirrorCS"),sQuery(id+"F0.wireOp",EDGE,"E28.MirrorCS"),sQuery(id+"F0.wireOp",EDGE,"E29.MirrorCS"),sQuery(id+"F0.wireOp",EDGE,"E30.MirrorCS"),sQuery(id+"F0.wireOp",EDGE,"E31.MirrorCS"),sQuery(id+"F0.wireOp",EDGE,"E32.MirrorCS")])]});
            hole(context, id + "F12", {"style" : HoleStyle.C_SINK, "holeDiameter" : 2 * mm, "cSinkDiameter" : 4 * mm, "endStyle" : HoleEndStyle.THROUGH, "locations" : qUnion([Q0, Q1, Q2, Q3]), "scope" : qUnion([Q4]), "cSinkAngle" : 90 * degree});
        }
        {
            var Q0;
            Q0=makeQuery(id+"F11.imprint","IMPRINT",FACE,{"disambiguationData":[TD([[makeQuery(id+"F11.imprint","IMPRINT",EDGE,{"derivedFrom":sQuery(id+"F11.wireOp",EDGE,"E53.bottom")}),-1.0]])]});
            var Q1;
            Q1=makeQuery(id+"F11.imprint","IMPRINT",FACE,{"disambiguationData":[TD([[makeQuery(id+"F11.imprint","IMPRINT",EDGE,{"derivedFrom":sQuery(id+"F11.wireOp",EDGE,"E58.MirrorCS")}),1.0]])]});
            var Q2;
            Q2=makeQuery(id+"F11.imprint","IMPRINT",FACE,{"disambiguationData":[TD([[makeQuery(id+"F11.imprint","IMPRINT",EDGE,{"derivedFrom":sQuery(id+"F11.wireOp",EDGE,"E62.MirrorCS")}),1.0]])]});
            var Q3;
            Q3=makeQuery(id+"F11.imprint","IMPRINT",FACE,{"disambiguationData":[TD([[makeQuery(id+"F11.imprint","IMPRINT",EDGE,{"derivedFrom":sQuery(id+"F11.wireOp",EDGE,"E54.MirrorCS")}),-1.0]])]});
            extrude(context, id + "F13", {"entities" : qUnion([Q0, Q1, Q2, Q3]), "operationType" : NewBodyOperationType.ADD, "depth" : 6 * mm});
        }
    });
